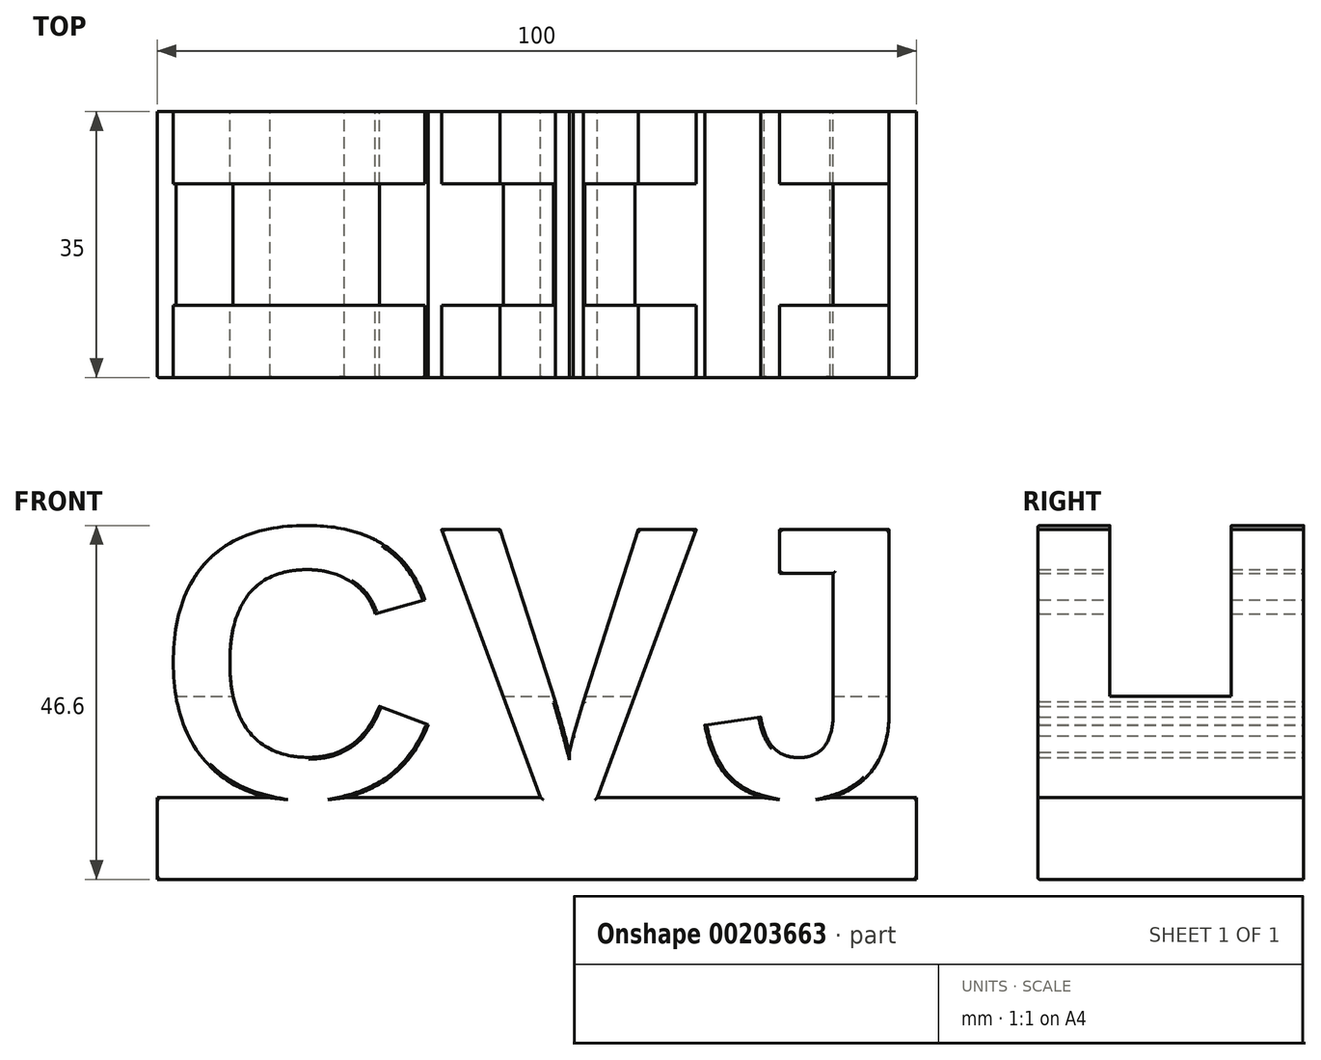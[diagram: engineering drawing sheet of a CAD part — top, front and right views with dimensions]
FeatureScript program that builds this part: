
annotation { "Feature Type Name" : "Feature", "Feature Type Description" : "" }
export const myFeature = defineFeature(function(context is Context, id is Id, definition is map)
    precondition{}
    {
        {
            var Q0;
            Q0=qCreatedBy(makeId("Front.planeOp"),FACE);
            var sketch = newSketch(context, id + "F4", { "sketchPlane" : qUnion([Q0])});
            skText(sketch, "E0", { "text": "CVJ", "fontName": "Arimo-Bold.ttf"});
            skLineSegment(sketch, "E1.bottom", {"start": v(-49.02, 0) * mm, "end": v(50.98, 0) * mm});
            skLineSegment(sketch, "E1.top", {"start": v(-49.02, -10.74) * mm, "end": v(50.98, -10.74) * mm});
            skLineSegment(sketch, "E1.left", {"start": v(-49.02, 0) * mm, "end": v(-49.02, -10.74) * mm});
            skLineSegment(sketch, "E1.right", {"start": v(50.98, 0) * mm, "end": v(50.98, -10.74) * mm});
            const initialGuessFtYCSxF4CX70OMJNh_0  = {"E0": [-0.04902, 0, 1, 0, 0.03698]};
            skSetInitialGuess(sketch, initialGuessFtYCSxF4CX70OMJNh_0);
            skSolve(sketch);
        }
        {
            var Q0;
            Q0 = qSketchRegion(id + "F4", true);
            extrude(context, id + "F0", {"entities" : qUnion([Q0]), "endBound" : BoundingType.SYMMETRIC, "depth" : 35 * mm});
        }
        {
            var Q0;
            Q0=qCreatedBy(makeId("Front.planeOp"),FACE);
            var sketch = newSketch(context, id + "F1", { "sketchPlane" : qUnion([Q0])});
            skLineSegment(sketch, "E2.bottom", {"start": v(-50.6, 36.24) * mm, "end": v(52.57, 36.24) * mm});
            skLineSegment(sketch, "E2.top", {"start": v(-50.6, 13.39) * mm, "end": v(52.57, 13.39) * mm});
            skLineSegment(sketch, "E2.left", {"start": v(-50.6, 36.24) * mm, "end": v(-50.6, 13.39) * mm});
            skLineSegment(sketch, "E2.right", {"start": v(52.57, 36.24) * mm, "end": v(52.57, 13.39) * mm});
            skSolve(sketch);
        }
        {
            var Q0;
            Q0=makeQuery(id+"F1.imprint","IMPRINT",FACE,{"disambiguationData":[TD([[makeQuery(id+"F1.imprint","IMPRINT",EDGE,{"derivedFrom":sQuery(id+"F1.wireOp",EDGE,"E2.bottom")}),-1.0]])]});
            extrude(context, id + "F2", {"entities" : qUnion([Q0]), "operationType" : NewBodyOperationType.REMOVE, "endBound" : BoundingType.SYMMETRIC, "oppositeDirection" : true, "depth" : 16 * mm});
        }
        {
            var Q0;
            Q0=makeQuery(id+"F0.opExtrude","CAP_FACE",FACE,{"disambiguationData":[OSD([sQuery(id+"F4.wireOp",EDGE,"E0.sketch_text.stroke-0"),sQuery(id+"F4.wireOp",EDGE,"E0.sketch_text.stroke-1"),sQuery(id+"F4.wireOp",EDGE,"E0.sketch_text.stroke-2"),sQuery(id+"F4.wireOp",EDGE,"E0.sketch_text.stroke-3"),sQuery(id+"F4.wireOp",EDGE,"E0.sketch_text.stroke-4"),sQuery(id+"F4.wireOp",EDGE,"E0.sketch_text.stroke-5"),sQuery(id+"F4.wireOp",EDGE,"E0.sketch_text.stroke-6"),sQuery(id+"F4.wireOp",EDGE,"E0.sketch_text.stroke-7"),sQuery(id+"F4.wireOp",EDGE,"E0.sketch_text.stroke-8"),sQuery(id+"F4.wireOp",EDGE,"E0.sketch_text.stroke-9"),sQuery(id+"F4.wireOp",EDGE,"E0.sketch_text.stroke-10"),sQuery(id+"F4.wireOp",EDGE,"E0.sketch_text.stroke-11"),sQuery(id+"F4.wireOp",EDGE,"E0.sketch_text.stroke-12"),sQuery(id+"F4.wireOp",EDGE,"E0.sketch_text.stroke-13"),sQuery(id+"F4.wireOp",EDGE,"E0.sketch_text.stroke-14"),sQuery(id+"F4.wireOp",EDGE,"E0.sketch_text.stroke-15"),sQuery(id+"F4.wireOp",EDGE,"E0.sketch_text.stroke-16"),sQuery(id+"F4.wireOp",EDGE,"E0.sketch_text.stroke-18"),sQuery(id+"F4.wireOp",EDGE,"E0.sketch_text.stroke-19"),sQuery(id+"F4.wireOp",EDGE,"E0.sketch_text.stroke-20"),sQuery(id+"F4.wireOp",EDGE,"E0.sketch_text.stroke-21"),sQuery(id+"F4.wireOp",EDGE,"E0.sketch_text.stroke-22"),sQuery(id+"F4.wireOp",EDGE,"E0.sketch_text.stroke-23"),sQuery(id+"F4.wireOp",EDGE,"E0.sketch_text.stroke-24"),sQuery(id+"F4.wireOp",EDGE,"E0.sketch_text.stroke-25"),sQuery(id+"F4.wireOp",EDGE,"E0.sketch_text.stroke-26"),sQuery(id+"F4.wireOp",EDGE,"E0.sketch_text.stroke-27"),sQuery(id+"F4.wireOp",EDGE,"E0.sketch_text.stroke-28"),sQuery(id+"F4.wireOp",EDGE,"E0.sketch_text.stroke-29"),sQuery(id+"F4.wireOp",EDGE,"E0.sketch_text.stroke-30"),sQuery(id+"F4.wireOp",EDGE,"E0.sketch_text.stroke-31"),sQuery(id+"F4.wireOp",EDGE,"E0.sketch_text.stroke-32"),sQuery(id+"F4.wireOp",EDGE,"E0.sketch_text.stroke-33"),sQuery(id+"F4.wireOp",EDGE,"E0.sketch_text.stroke-34"),sQuery(id+"F4.wireOp",EDGE,"E0.sketch_text.stroke-35"),sQuery(id+"F4.wireOp",EDGE,"E0.sketch_text.stroke-36"),sQuery(id+"F4.wireOp",EDGE,"E0.sketch_text.stroke-37"),sQuery(id+"F4.wireOp",EDGE,"E0.sketch_text.stroke-38"),sQuery(id+"F4.wireOp",EDGE,"E0.sketch_text.stroke-39"),sQuery(id+"F4.wireOp",EDGE,"E0.sketch_text.stroke-40"),sQuery(id+"F4.wireOp",EDGE,"E1.bottom"),sQuery(id+"F4.wireOp",EDGE,"E1.top"),sQuery(id+"F4.wireOp",EDGE,"E1.left"),sQuery(id+"F4.wireOp",EDGE,"E1.right")])],"isStart":false});
            fillet(context, id + "F3", {"entities" : qUnion([Q0]), "radius" : .25 * mm, "tangentPropagation" : true, "allowEdgeOverflow" : false});
        }
    });
